# Revit family: G 6060 EPM
name_source: partatom
category: Lighting Fixtures
revit_build: Autodesk Revit 2017 (Build: 20160225_1515(x64)
units: mm (PartAtom-declared; Revit-internal decimal feet)

## family parameters
Cut with Voids When Loaded = No
Host = Face
Light Source = Yes
Part Type = Normal
Room Calculation Point = No
Round Connector Dimension = Use Diameter
Shared = No

## types (6) — shared parameters
Color Filter = 16777215
Default Elevation = 1219 mm
Description = Microprismatic Diffuser
Dimming Lamp Color Temperature Shift = <None>
Emit Shape Visible in Rendering = Yes
Emit from Rectangle Length = 555 mm  [stored 1.82087 ft]
Emit from Rectangle Width = 555 mm  [stored 1.82087 ft]
Lamp = LED
Manufacturer = ARLIGHT
Model = G6060EPM
Tilt Angle = 90.00°
Type Comments = ELEGANT PRO
Type Image = <None>

## per-type parameters (varying)
| type | Apparent Load | Photometric Web File | Wattage Comments |
| GEPM.6060.27.30 | 26 VA | g-6060-epm-27w-3k-80ra-sa-07.ies | 27W |
| GEPM.6060.27.40 | 26 VA | g-6060-epm-27w-4k-80ra-sa-07.ies | 27W |
| GEPM.6060.20.30 | 19 VA | g-6060-epm-19w-3k-80ra-sa-05.ies | 20W |
| GEPM.6060.20.40 | 19 VA | g-6060-epm-19w-4k-80ra-sa-05.ies | 20W |
| GEPM.6060.36.30 | 36 VA | g-6060-epm-35w-3k-80ra-sa-09.ies | 36W |
| GEPM.6060.36.40 | 36 VA | g-6060-epm-35w-4k-80ra-sa-09.ies | 36W |

note: [stored X ft] marks values corroborated as IEEE doubles in the binary element streams (Revit-internal decimal feet)

## geometry (parser evidence)
native form markers: Sweep x1
no freeform markers — native parametric forms only
